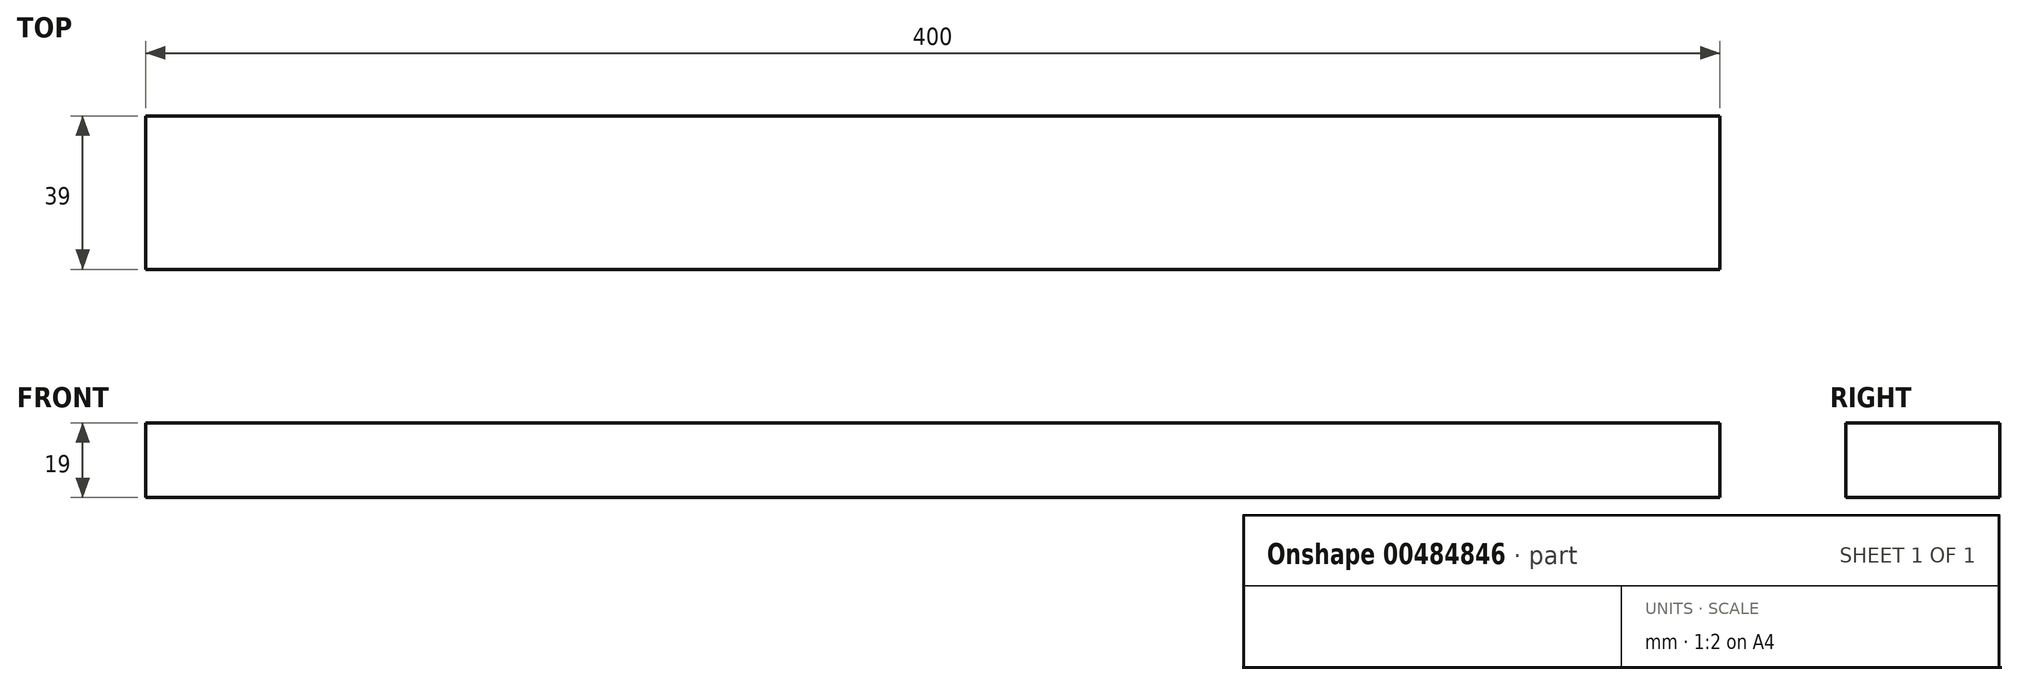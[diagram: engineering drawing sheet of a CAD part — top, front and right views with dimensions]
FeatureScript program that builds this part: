
annotation { "Feature Type Name" : "Feature", "Feature Type Description" : "" }
export const myFeature = defineFeature(function(context is Context, id is Id, definition is map)
    precondition{}
    {
        {
            var Q0;
            Q0=qCreatedBy(makeId("Top.planeOp"),FACE);
            var sketch = newSketch(context, id + "F0", { "sketchPlane" : qUnion([Q0])});
            skLineSegment(sketch, "E0.bottom", {"start": v(-163.17, 20.57) * mm, "end": v(236.83, 20.57) * mm});
            skLineSegment(sketch, "E0.top", {"start": v(-163.17, -18.43) * mm, "end": v(236.83, -18.43) * mm});
            skLineSegment(sketch, "E0.left", {"start": v(-163.17, 20.57) * mm, "end": v(-163.17, -18.43) * mm});
            skLineSegment(sketch, "E0.right", {"start": v(236.83, 20.57) * mm, "end": v(236.83, -18.43) * mm});
            skSolve(sketch);
        }
        {
            var Q0;
            Q0 = qSketchRegion(id + "F0", true);
            extrude(context, id + "F1", {"entities" : qUnion([Q0]), "depth" : 19 * mm});
        }
    });
